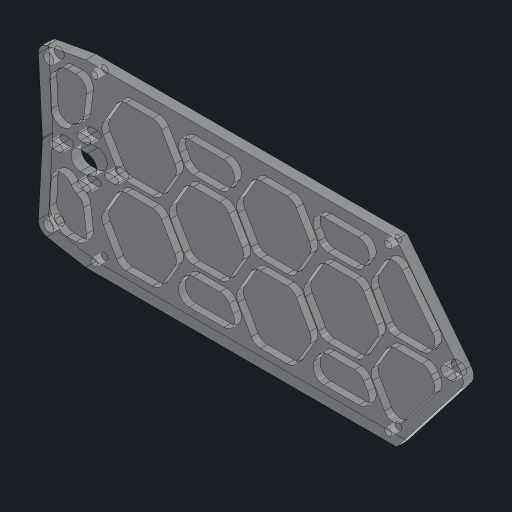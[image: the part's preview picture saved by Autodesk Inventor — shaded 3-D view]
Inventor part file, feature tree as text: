
AUTODESK INVENTOR PART (.ipt)
format: ipt  version: 2023.2 (Build 272271030, 271C)  size: 670,208 bytes
history: native  units: mm
features: extrude x2, fillet x2, mirror x2, sketch x2, projected_geometry x1
ambient origin geometry x8: Origin, YZ Plane, XZ Plane, XY Plane, X Axis, Y Axis, Z Axis, Center Point
bodies: Solid1 (feature_tree)
feature tree (9):
  extrude  "Extrusion1"  Depth=42.0mm
  extrude  "Extrusion6"  Depth=22.0mm
  fillet  "Fillet4"  Radius=36.0mm
  mirror  "Mirror3"
  mirror  "Mirror4"
  fillet  "Fillet5"  Radius=127.0mm
  sketch  "Sketch1"  dims[d0=90.0mm d1=42.0mm]
  sketch  "Sketch6"  dims[d2=5.0mm d3=22.0mm d5=36.0mm d6=127.0mm d7=8.0mm d8=8.0mm d9=0.0mm d10=3.0mm d11=3.0mm d12=8.0mm d13=3.0mm d14=1.5mm d15=8.5mm d16=1.25mm d17=5.0mm d18=5.0mm d19=1.0mm d20=5.5mm d21=16.0mm d22=12.0mm d23=1.0mm d24=1.0mm d25=1.0mm d26=2.0mm d27=1.0mm d28=2.0mm d29=2.0mm d30=2.0mm d31=2.0mm d32=2.0mm d33=2.0mm d34=5.0mm d35=5.0mm d36=5.0mm d37=1.5mm d38=1.5mm d39=3.0mm d40=0.0mm d102=2.0mm d103=2.5mm d104=2.5mm d105=2.5mm d106=2.5mm d111=3.0mm d113=5.0mm d114=3.0mm d115=5.0mm d116=2.0mm d117=2.0mm d118=2.0mm d119=2.0mm d120=6.2mm d121=3.0mm d122=3.0mm d123=3.0mm d124=3.0mm d125=1.5mm d126=3.0mm d127=3.0mm d128=38.971143mm d129=2.0mm d130=0.0mm d131=30.0mm d133=38.971143mm d134=10.0mm d136=10.0mm d138=3.1mm d139=3.1mm d140=0.872665mm d141=0.5mm d142=0.872665mm]
  projected_geometry  "Projected Loop6"
